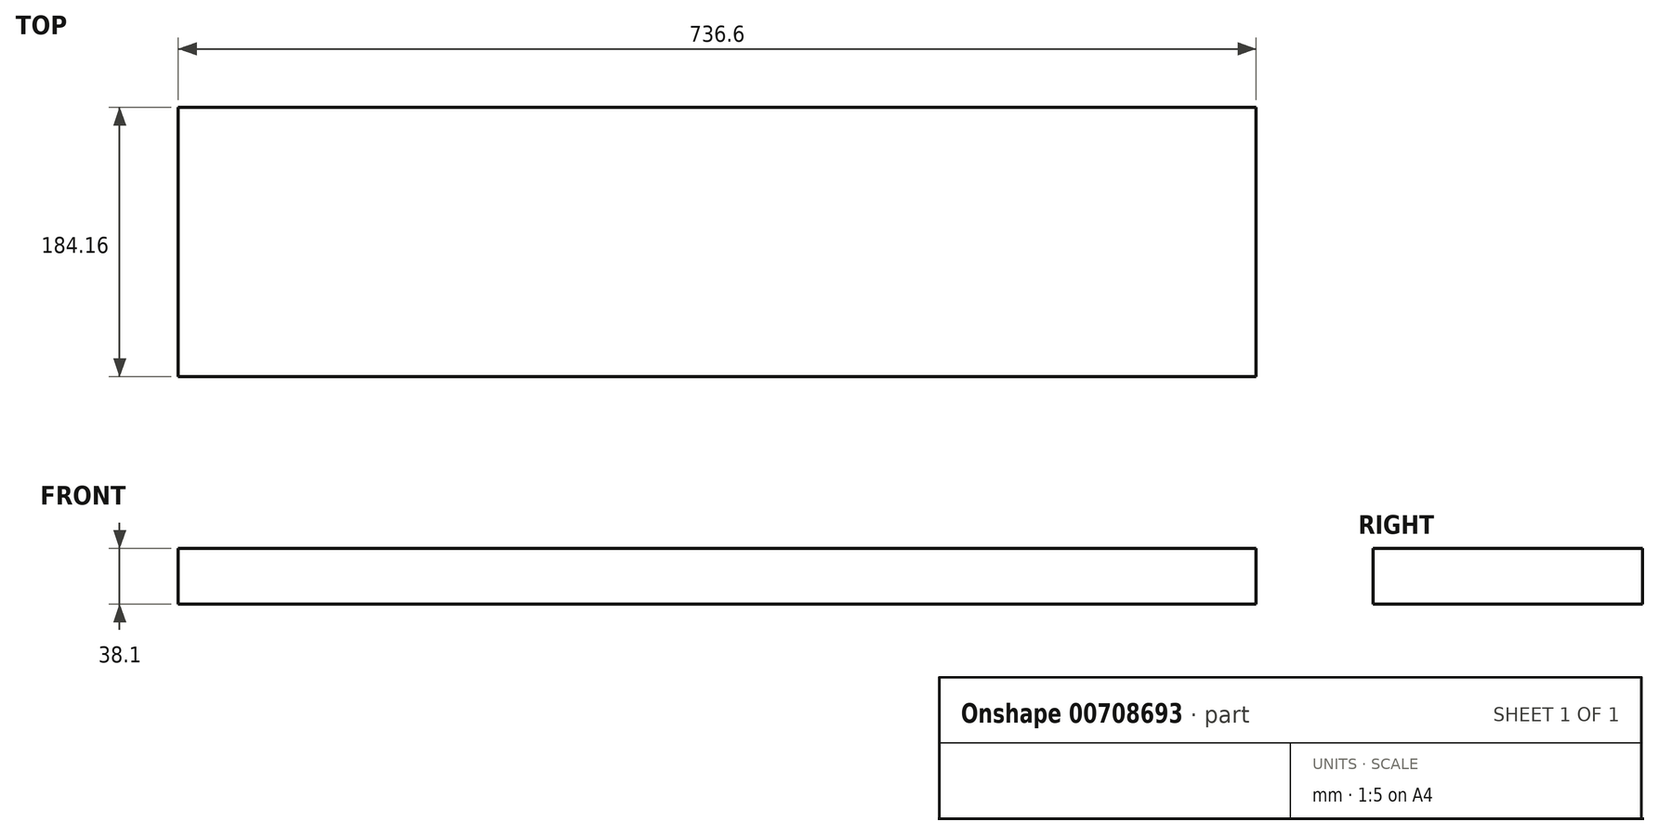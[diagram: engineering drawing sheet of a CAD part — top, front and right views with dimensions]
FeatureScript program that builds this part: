
annotation { "Feature Type Name" : "Feature", "Feature Type Description" : "" }
export const myFeature = defineFeature(function(context is Context, id is Id, definition is map)
    precondition{}
    {
        {
            var Q0;
            Q0=qCreatedBy(makeId("Right.planeOp"),FACE);
            var sketch = newSketch(context, id + "F0", { "sketchPlane" : qUnion([Q0])});
            skLineSegment(sketch, "E0.bottom", {"start": v(92.07, -19.05) * mm, "end": v(-92.07, -19.05) * mm});
            skLineSegment(sketch, "E0.top", {"start": v(92.07, 19.05) * mm, "end": v(-92.07, 19.05) * mm});
            skLineSegment(sketch, "E0.left", {"start": v(92.07, -19.05) * mm, "end": v(92.07, 19.05) * mm});
            skLineSegment(sketch, "E0.right", {"start": v(-92.07, -19.05) * mm, "end": v(-92.07, 19.05) * mm});
            skPoint(sketch, "E0.middle", {"position": v(0, 0) * mm});
            skSolve(sketch);
        }
        {
            var Q0;
            Q0=makeQuery(id+"F0.imprint","IMPRINT",FACE,{"disambiguationData":[TD([[makeQuery(id+"F0.imprint","IMPRINT",EDGE,{"derivedFrom":sQuery(id+"F0.wireOp",EDGE,"E0.bottom")}),-1.0]])]});
            extrude(context, id + "F1", {"entities" : qUnion([Q0]), "endBound" : BoundingType.SYMMETRIC, "depth" : 736.6 * mm, "offsetDistance" : 25.4 * mm});
        }
    });
